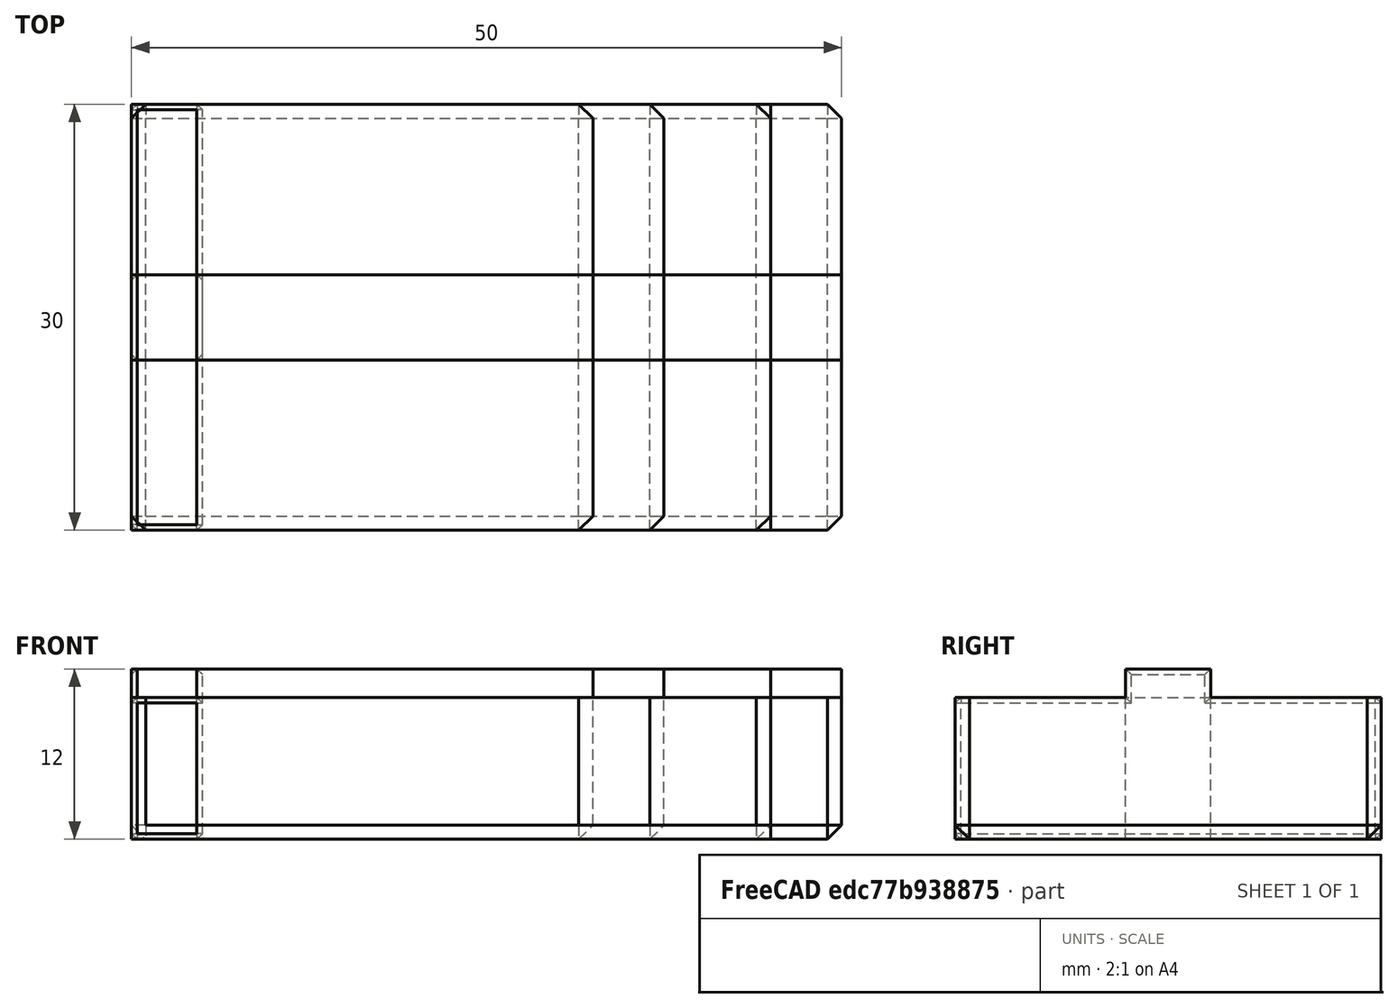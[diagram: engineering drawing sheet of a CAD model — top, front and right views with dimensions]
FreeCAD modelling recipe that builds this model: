
FCSTD DOCUMENT  (FreeCAD 0.18R16146 (Git))
Label: spacer
License: All rights reserved
LicenseURL: http://en.wikipedia.org/wiki/All_rights_reserved
objects: Part::Box×10, Part::Chamfer×5, Part::MultiFuse×4, Part::Feature×1
note: 20 computed .brp shape members not serialized (recipe doc carries the construction recipe); baked Part::Feature solids carry a one-line shape summary decoded from their .brp

FEATURE [Part::Box] Box  label="Cube"
  AttacherType = Attacher::AttachEngine3D
  Height = 10
  Length = 50
  Width = 30
FEATURE [Part::Box] Box001  label="Cube001"
  AttacherType = Attacher::AttachEngine3D
  Height = 12
  Length = 50
  Placement = pos=(0,12,0) rot=(0,0,1;0rad)
  Width = 6
FEATURE [Part::Box] Box002  label="Cube002"
  AttacherType = Attacher::AttachEngine3D
  Height = 12
  Length = 45
  Placement = pos=(0,12,0) rot=(0,0,1;0rad)
  Width = 6
FEATURE [Part::Box] Box003  label="Cube003"
  AttacherType = Attacher::AttachEngine3D
  Height = 10
  Length = 45
  Width = 30
FEATURE [Part::MultiFuse] Fusion  label="tdfrs"
  Shapes = -> [Box001,Box]
FEATURE [Part::Box] Box004  label="Cube004"
  AttacherType = Attacher::AttachEngine3D
  Height = 12
  Length = 45
  Placement = pos=(0,12,0) rot=(0,0,1;0rad)
  Width = 6
FEATURE [Part::Box] Box005  label="Cube005"
  AttacherType = Attacher::AttachEngine3D
  Height = 10
  Length = 45
  Width = 30
FEATURE [Part::MultiFuse] Fusion001
  Shapes = -> [Box005,Box004]
FEATURE [Part::Chamfer] Chamfer  label="50-spacer"
  Base = -> Fusion
  Edges = 12 edges r=1: [Edge4,Edge6,Edge7,Edge12,Edge13,Edge15,Edge20,Edge21,Edge22,Edge31,Edge32,Edge33]
FEATURE [Part::Chamfer] Chamfer001  label="45-spacer"
  Base = -> Fusion001
  Edges = 12 edges r=1: [Edge3,Edge4,Edge10,Edge12,Edge13,Edge14,Edge22,Edge23,Edge25,Edge34,Edge35,Edge36]
FEATURE [Part::Feature] Fusion002001  label="Fusion003"
  shape: bbox 5 x 30 x 12 mm, 10 faces (baked)
FEATURE [Part::Chamfer] Chamfer002  label="05-spacer"
  Base = -> Fusion002001
  Edges = 20 edges r=0.4: [Edge1,Edge3,Edge4,Edge5,Edge6,Edge7,Edge8,Edge10,Edge11,Edge13,Edge14,Edge15,Edge17,Edge18,Edge19,Edge20,Edge21,Edge22,Edge23,Edge24]
FEATURE [Part::Box] Box006  label="Cube006"
  AttacherType = Attacher::AttachEngine3D
  Height = 12
  Length = 32.5
  Placement = pos=(0,12,0) rot=(0,0,1;0rad)
  Width = 6
FEATURE [Part::Box] Box007  label="Cube007"
  AttacherType = Attacher::AttachEngine3D
  Height = 10
  Length = 32.5
  Width = 30
FEATURE [Part::MultiFuse] Fusion002002
  Shapes = -> [Box007,Box006]
FEATURE [Part::Box] Box008  label="Cube008"
  AttacherType = Attacher::AttachEngine3D
  Height = 12
  Length = 37.5
  Placement = pos=(0,12,0) rot=(0,0,1;0rad)
  Width = 6
FEATURE [Part::Box] Box009  label="Cube009"
  AttacherType = Attacher::AttachEngine3D
  Height = 10
  Length = 37.5
  Width = 30
FEATURE [Part::MultiFuse] Fusion002003
  Shapes = -> [Box009,Box008]
FEATURE [Part::Chamfer] Chamfer003  label="325-spacer"
  Base = -> Fusion002002
  Edges = 12 edges r=1: [Edge3,Edge4,Edge10,Edge12,Edge13,Edge14,Edge22,Edge23,Edge25,Edge34,Edge35,Edge36]
FEATURE [Part::Chamfer] Chamfer004  label="375-spacer"
  Base = -> Fusion002003
  Edges = 12 edges r=1: [Edge3,Edge4,Edge10,Edge12,Edge13,Edge14,Edge22,Edge23,Edge25,Edge34,Edge35,Edge36]
